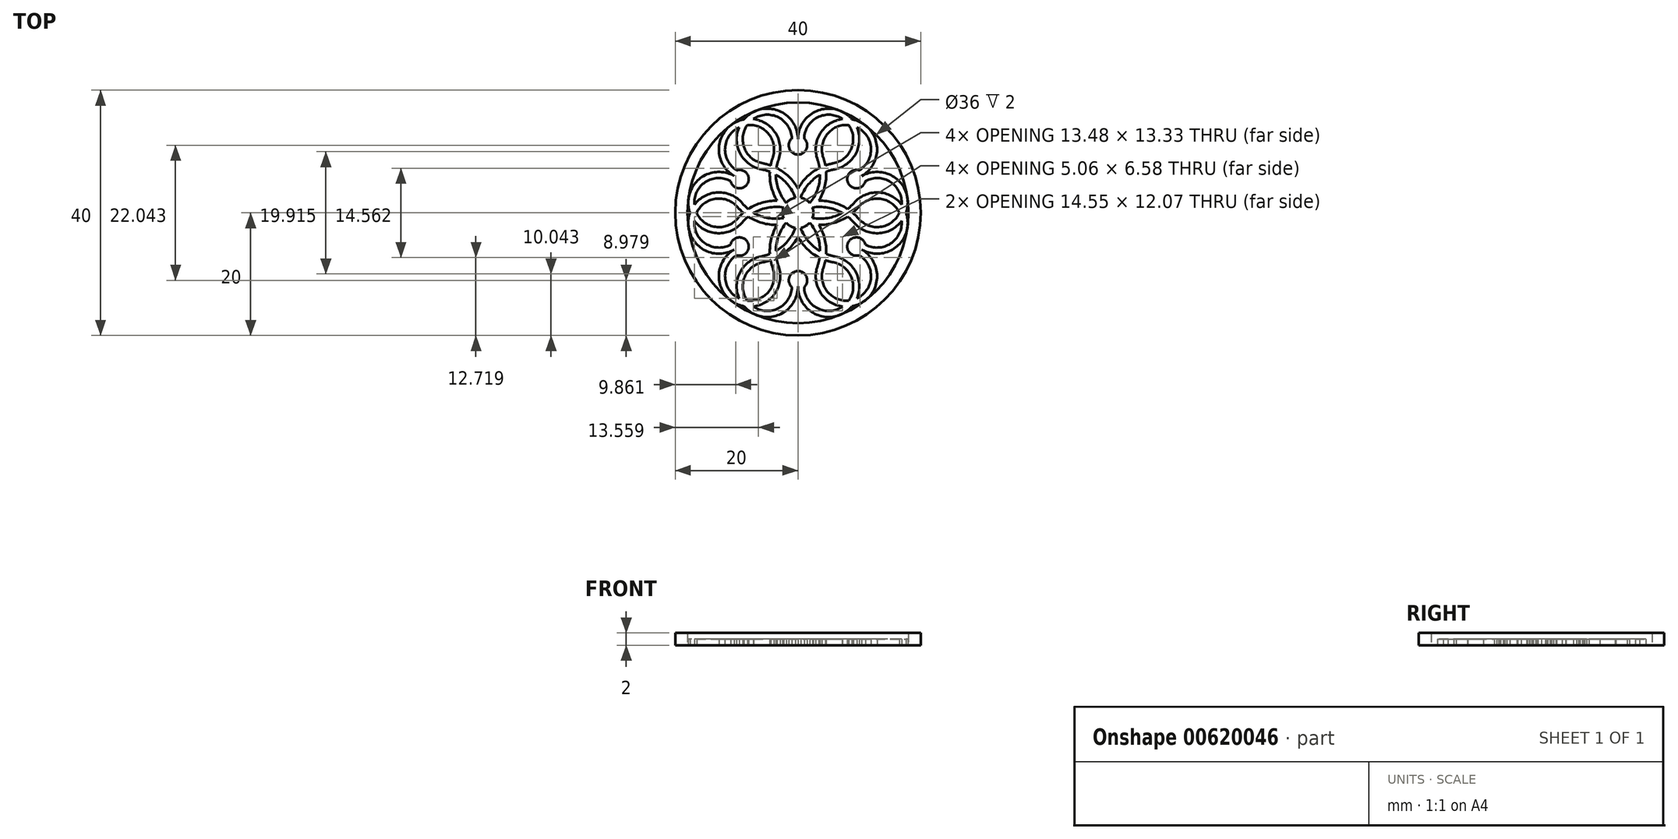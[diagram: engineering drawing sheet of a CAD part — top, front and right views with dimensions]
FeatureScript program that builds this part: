
annotation { "Feature Type Name" : "Feature", "Feature Type Description" : "" }
export const myFeature = defineFeature(function(context is Context, id is Id, definition is map)
    precondition{}
    {
        {
            var Q0;
            Q0=qCreatedBy(makeId("Top.planeOp"),FACE);
            var sketch = newSketch(context, id + "F0", { "sketchPlane" : qUnion([Q0])});
            skCircle(sketch, "E0", {"center": v(0, 0) * mm, "radius": 20 * mm});
            skArc(sketch, "E1", {"start": v(0, 12) * mm, "mid": v(-8.2, 15.84) * mm, "end": v(-5.9, 7.08) * mm});
            skPoint(sketch, "E1.second.point", {"position": v(0, 12) * mm});
            skLineSegment(sketch, "E2", {"start": v(-5, 12) * mm, "end": v(-5.9, 7.08) * mm, "construction": true});
            skLineSegment(sketch, "E3", {"start": v(-5.9, 7.08) * mm, "end": v(-5.9, 7.08) * mm});
            skArc(sketch, "E4", {"start": v(-5.9, 7.08) * mm, "mid": v(-1.67, 4.6) * mm, "end": v(0, 0) * mm});
            skCircle(sketch, "E5", {"center": v(0, 0) * mm, "radius": 2.5 * mm});
            skCircle(sketch, "E6", {"center": v(0, 0) * mm, "radius": 18 * mm});
            skLineSegment(sketch, "E7", {"start": v(0, 0) * mm, "end": v(0, 20) * mm, "construction": true});
            skArc(sketch, "E8.MirrorCS", {"start": v(5.9, 7.08) * mm, "mid": v(1.67, 4.6) * mm, "end": v(0, 0) * mm});
            skLineSegment(sketch, "E9.MirrorCS", {"start": v(5.9, 7.08) * mm, "end": v(5.9, 7.08) * mm});
            skArc(sketch, "E10.MirrorCS", {"start": v(0, 12) * mm, "mid": v(8.2, 15.84) * mm, "end": v(5.9, 7.08) * mm});
            skArc(sketch, "E11.0", {"start": v(-1, 12.12) * mm, "mid": v(-7.6, 15.04) * mm, "end": v(-5.72, 8.07) * mm});
            skLineSegment(sketch, "E12.0", {"start": v(-5.72, 8.07) * mm, "end": v(-5.72, 8.07) * mm});
            skArc(sketch, "E12.1", {"start": v(1, 12.12) * mm, "mid": v(7.6, 15.04) * mm, "end": v(5.72, 8.07) * mm});
            skLineSegment(sketch, "E12.2", {"start": v(5.72, 8.07) * mm, "end": v(5.72, 8.07) * mm});
            skArc(sketch, "E12.3", {"start": v(5.72, 8.07) * mm, "mid": v(2.4, 6.64) * mm, "end": v(0, 3.92) * mm});
            skArc(sketch, "E12.4", {"start": v(-5.72, 8.07) * mm, "mid": v(-2.4, 6.64) * mm, "end": v(0, 3.92) * mm});
            skCircle(sketch, "E13", {"center": v(0, 11) * mm, "radius": 1.5 * mm});
            skPoint(sketch, "E14", {"position": v(0, 10) * mm});
            skSolve(sketch);
        }
        {
            var Q0;
            Q0=qCreatedBy(makeId("Right.planeOp"),FACE);
            var sketch = newSketch(context, id + "F1", { "sketchPlane" : qUnion([Q0])});
            skLineSegment(sketch, "E15", {"start": v(0, 0) * mm, "end": v(0, 13.72) * mm, "construction": true});
            skSolve(sketch);
        }
        {
            var Q0;
            Q0=makeQuery(id+"F0.imprint","IMPRINT",FACE,{"disambiguationData":[TD([[makeQuery(id+"F0.imprint","IMPRINT",EDGE,{"derivedFrom":sQuery(id+"F0.wireOp",EDGE,"E0")}),1.0]])]});
            extrude(context, id + "F2", {"entities" : qUnion([Q0]), "depth" : 2 * mm, "offsetDistance" : 25 * mm});
        }
        {
            var Q0;
            {var subQ15=sQuery(id+"F0.wireOp",EDGE,"E11.0");Q0=makeQuery(id+"F0.imprint","IMPRINT",FACE,{"disambiguationData":[TD([[makeQuery(id+"F0.imprint","IMPRINT",EDGE,{"derivedFrom":subQ15}),-1.0]])]});}
            var Q1;
            {var subQ2=sQuery(id+"F0.wireOp",EDGE,"E10.MirrorCS");var subQ4=sQuery(id+"F0.wireOp",EDGE,"E1");var subQ5=makeQuery(id+"F0.imprint","INTERSECT",VERTEX,{"derivedFrom":[subQ4,subQ2]});Q1=makeQuery(id+"F0.imprint","IMPRINT",FACE,{"disambiguationData":[TD([[makeQuery(id+"F0.imprint","IMPRINT",EDGE,{"disambiguationData":[TD([[subQ5,-1.0]])],"derivedFrom":subQ4}),1.0]])]});}
            extrude(context, id + "F3", {"entities" : qUnion([Q0, Q1]), "operationType" : NewBodyOperationType.ADD, "depth" : 1 * mm, "offsetDistance" : 25 * mm});
        }
        {
            var Q0;
            Q0=makeQuery(id+"F3.opExtrude","SWEPT_BODY",BODY,{"disambiguationData":[OSD([sQuery(id+"F0.wireOp",EDGE,"E1"),sQuery(id+"F0.wireOp",EDGE,"E3"),sQuery(id+"F0.wireOp",EDGE,"E4"),sQuery(id+"F0.wireOp",EDGE,"E5"),sQuery(id+"F0.wireOp",EDGE,"E8.MirrorCS"),sQuery(id+"F0.wireOp",EDGE,"E9.MirrorCS"),sQuery(id+"F0.wireOp",EDGE,"E10.MirrorCS"),sQuery(id+"F0.wireOp",EDGE,"E11.0"),sQuery(id+"F0.wireOp",EDGE,"E12.0"),sQuery(id+"F0.wireOp",EDGE,"E12.1"),sQuery(id+"F0.wireOp",EDGE,"E12.2"),sQuery(id+"F0.wireOp",EDGE,"E12.3"),sQuery(id+"F0.wireOp",EDGE,"E12.4"),sQuery(id+"F0.wireOp",EDGE,"E13")])]});
            var Q1;
            Q1=sQuery(id+"F1.wireOp",EDGE,"E15");
            circularPattern(context, id + "F4", {"operationType" : NewBodyOperationType.ADD, "entities" : qUnion([Q0]), "axis" : qUnion([Q1]), "angle" : 360 * degree, "instanceCount" : 6, "equalSpace" : true});
        }
        {
            var Q0;
            {var subQ1=sQuery(id+"F0.wireOp",EDGE,"E4");var subQ3=sQuery(id+"F0.wireOp",EDGE,"E5");var subQ4=makeQuery(id+"F0.imprint","INTERSECT",VERTEX,{"derivedFrom":[subQ1,subQ3]});Q0=makeQuery(id+"F0.imprint","IMPRINT",FACE,{"disambiguationData":[TD([[makeQuery(id+"F0.imprint","IMPRINT",EDGE,{"disambiguationData":[TD([[subQ4,-1.0]])],"derivedFrom":subQ3}),1.0]])]});}
            var Q1;
            {var subQ0=sQuery(id+"F0.wireOp",EDGE,"7829a788-bc4e-437e-802b-f932468686cc.1.3");var subQ1=sQuery(id+"F0.wireOp",EDGE,"E5");var subQ2=makeQuery(id+"F0.imprint","INTERSECT",VERTEX,{"derivedFrom":[subQ1,subQ0]});Q1=makeQuery(id+"F0.imprint","IMPRINT",FACE,{"disambiguationData":[TD([[makeQuery(id+"F0.imprint","IMPRINT",EDGE,{"disambiguationData":[TD([[subQ2,-1.0]])],"derivedFrom":subQ1}),1.0]])]});}
            var Q2;
            {var subQ0=sQuery(id+"F0.wireOp",EDGE,"7829a788-bc4e-437e-802b-f932468686cc.1.2");var subQ1=sQuery(id+"F0.wireOp",EDGE,"E5");var subQ2=makeQuery(id+"F0.imprint","INTERSECT",VERTEX,{"derivedFrom":[subQ1,subQ0]});Q2=makeQuery(id+"F0.imprint","IMPRINT",FACE,{"disambiguationData":[TD([[makeQuery(id+"F0.imprint","IMPRINT",EDGE,{"disambiguationData":[TD([[subQ2,-1.0]])],"derivedFrom":subQ1}),1.0]])]});}
            var Q3;
            {var subQ0=sQuery(id+"F0.wireOp",EDGE,"7829a788-bc4e-437e-802b-f932468686cc.2.3");var subQ1=sQuery(id+"F0.wireOp",EDGE,"E5");var subQ2=makeQuery(id+"F0.imprint","INTERSECT",VERTEX,{"derivedFrom":[subQ1,subQ0]});Q3=makeQuery(id+"F0.imprint","IMPRINT",FACE,{"disambiguationData":[TD([[makeQuery(id+"F0.imprint","IMPRINT",EDGE,{"disambiguationData":[TD([[subQ2,-1.0]])],"derivedFrom":subQ1}),1.0]])]});}
            var Q4;
            {var subQ0=sQuery(id+"F0.wireOp",EDGE,"7829a788-bc4e-437e-802b-f932468686cc.2.2");var subQ1=sQuery(id+"F0.wireOp",EDGE,"E5");var subQ2=makeQuery(id+"F0.imprint","INTERSECT",VERTEX,{"derivedFrom":[subQ1,subQ0]});Q4=makeQuery(id+"F0.imprint","IMPRINT",FACE,{"disambiguationData":[TD([[makeQuery(id+"F0.imprint","IMPRINT",EDGE,{"disambiguationData":[TD([[subQ2,-1.0]])],"derivedFrom":subQ1}),1.0]])]});}
            var Q5;
            {var subQ0=sQuery(id+"F0.wireOp",EDGE,"7829a788-bc4e-437e-802b-f932468686cc.3.2");var subQ1=sQuery(id+"F0.wireOp",EDGE,"E5");var subQ2=makeQuery(id+"F0.imprint","INTERSECT",VERTEX,{"derivedFrom":[subQ1,subQ0]});Q5=makeQuery(id+"F0.imprint","IMPRINT",FACE,{"disambiguationData":[TD([[makeQuery(id+"F0.imprint","IMPRINT",EDGE,{"disambiguationData":[TD([[subQ2,1.0]])],"derivedFrom":subQ1}),1.0]])]});}
            var Q6;
            {var subQ0=sQuery(id+"F0.wireOp",EDGE,"E8.MirrorCS");var subQ1=sQuery(id+"F0.wireOp",EDGE,"E5");var subQ2=makeQuery(id+"F0.imprint","INTERSECT",VERTEX,{"derivedFrom":[subQ1,subQ0]});Q6=makeQuery(id+"F0.imprint","IMPRINT",FACE,{"disambiguationData":[TD([[makeQuery(id+"F0.imprint","IMPRINT",EDGE,{"disambiguationData":[TD([[subQ2,1.0]])],"derivedFrom":subQ1}),1.0]])]});}
            var Q7;
            {var subQ1=sQuery(id+"F0.wireOp",EDGE,"E4");var subQ3=sQuery(id+"F0.wireOp",EDGE,"E5");var subQ4=makeQuery(id+"F0.imprint","INTERSECT",VERTEX,{"derivedFrom":[subQ1,subQ3]});Q7=makeQuery(id+"F0.imprint","IMPRINT",FACE,{"disambiguationData":[TD([[makeQuery(id+"F0.imprint","IMPRINT",EDGE,{"disambiguationData":[TD([[subQ4,1.0]])],"derivedFrom":subQ3}),1.0]])]});}
            extrude(context, id + "F5", {"entities" : qUnion([Q0, Q1, Q2, Q3, Q4, Q5, Q6, Q7]), "operationType" : NewBodyOperationType.ADD, "depth" : 1 * mm, "offsetDistance" : 25 * mm});
        }
    });
